# Revit family: Sanitary_Showers_hansgrohe_60090XXX-RainDrain-Staro-Basic-set-for-waste-set-for-shower-tray_NEW
name_source: partatom
category: Plumbing Fixtures
units: mm (PartAtom-declared; Revit-internal decimal feet)

## family parameters
Cut with Voids When Loaded = Yes
Host = Face
Maintain Annotation Orientation = No
OmniClass Number = 23.31.17.29
OmniClass Title = Shower Drains
Part Type = Normal
Room Calculation Point = No
Round Connector Dimension = Use Diameter
Shared = No

## types (1)
- 60090XXX RainDrain Staro Basic set for waste set for shower tray
    Connector Description = Water Outlet 50 mm
    Default Elevation = 1219 mm
    Description = RainDrain Staro Basic set for waste set for shower tray
    Diameter = 50 mm  [stored 0.164042 ft]
    Manufacturer = Hansgrohe
    Material 1 = Hansgrohe - Metal - Chrome
    Material 2 = Hansgrohe - Plastic - Black
    Model = 60090XXX
    Product Page URL = https://www.hansgrohe.com
    Product data url = https://bimobject.com
    URL = https://www.hansgrohe.com
    Version = 1

note: [stored X ft] marks values corroborated as IEEE doubles in the binary element streams (Revit-internal decimal feet)

## geometry (parser evidence)
native form markers: Sweep x2
no freeform markers — native parametric forms only
